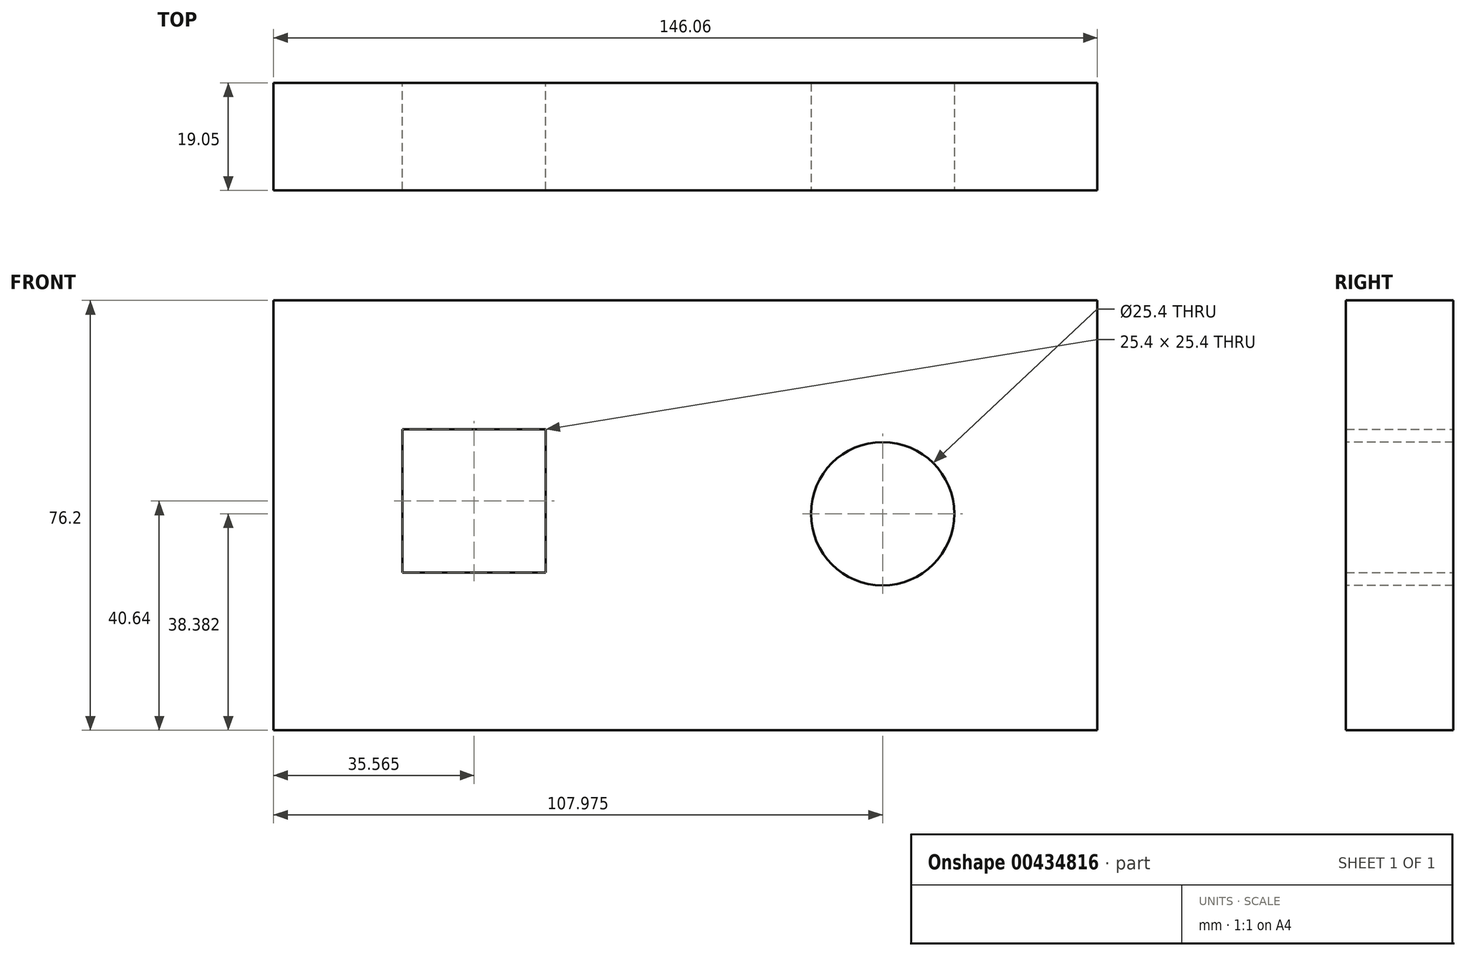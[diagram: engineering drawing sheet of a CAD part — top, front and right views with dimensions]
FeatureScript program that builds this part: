
annotation { "Feature Type Name" : "Feature", "Feature Type Description" : "" }
export const myFeature = defineFeature(function(context is Context, id is Id, definition is map)
    precondition{}
    {
        {
            var Q0;
            Q0=qCreatedBy(makeId("Front.planeOp"),FACE);
            var sketch = newSketch(context, id + "F0", { "sketchPlane" : qUnion([Q0])});
            skLineSegment(sketch, "E0.bottom", {"start": v(0, 0) * mm, "end": v(-73.03, 0) * mm});
            skLineSegment(sketch, "E0.top", {"start": v(0, 76.2) * mm, "end": v(-73.03, 76.2) * mm});
            skLineSegment(sketch, "E0.left", {"start": v(0, 0) * mm, "end": v(0, 76.2) * mm});
            skLineSegment(sketch, "E0.right", {"start": v(-73.03, 0) * mm, "end": v(-73.03, 76.2) * mm});
            skLineSegment(sketch, "E1.bottom", {"start": v(0, 0) * mm, "end": v(73.03, 0) * mm});
            skLineSegment(sketch, "E1.top", {"start": v(0, 76.2) * mm, "end": v(73.02, 76.2) * mm});
            skLineSegment(sketch, "E1.right", {"start": v(73.03, 0) * mm, "end": v(73.02, 76.2) * mm});
            skSolve(sketch);
        }
        {
            var Q0;
            Q0=makeQuery(id+"F0.imprint","IMPRINT",FACE,{"disambiguationData":[TD([[makeQuery(id+"F0.imprint","IMPRINT",EDGE,{"derivedFrom":sQuery(id+"F0.wireOp",EDGE,"E0.bottom")}),-1.0]])]});
            var sketch = newSketch(context, id + "F1", { "sketchPlane" : qUnion([Q0])});
            skLineSegment(sketch, "E2.bottom", {"start": v(-50.17, 53.34) * mm, "end": v(-24.77, 53.34) * mm});
            skLineSegment(sketch, "E2.top", {"start": v(-50.16, 27.94) * mm, "end": v(-24.77, 27.94) * mm});
            skLineSegment(sketch, "E2.left", {"start": v(-50.16, 53.34) * mm, "end": v(-50.16, 27.94) * mm});
            skLineSegment(sketch, "E2.right", {"start": v(-24.77, 53.34) * mm, "end": v(-24.76, 27.94) * mm});
            skSolve(sketch);
        }
        {
            var Q0;
            Q0=makeQuery(id+"F0.imprint","IMPRINT",FACE,{"disambiguationData":[TD([[makeQuery(id+"F0.imprint","IMPRINT",EDGE,{"derivedFrom":sQuery(id+"F0.wireOp",EDGE,"E1.bottom")}),1.0]])]});
            extrude(context, id + "F2", {"entities" : qUnion([Q0]), "depth" : 19.05 * mm});
        }
        {
            var Q0;
            Q0=makeQuery(id+"F1.imprint","IMPRINT",FACE,{"disambiguationData":[TD([[makeQuery(id+"F1.imprint","IMPRINT",EDGE,{"derivedFrom":sQuery(id+"F1.wireOp",EDGE,"E2.bottom")}),1.0]])]});
            extrude(context, id + "F3", {"entities" : qUnion([Q0]), "operationType" : NewBodyOperationType.ADD, "depth" : 19.05 * mm});
        }
        {
            var Q0;
            {var subQ0=sQuery(id+"F0.wireOp",EDGE,"E0.left");Q0=makeQuery(id+"F3.boolean.opBoolean","MERGE",FACE,{"derivedFrom":[makeQuery(id+"F2.opExtrude","CAP_FACE",FACE,{"disambiguationData":[OSD([sQuery(id+"F0.wireOp",EDGE,"E1.bottom"),sQuery(id+"F0.wireOp",EDGE,"E1.top"),subQ0,sQuery(id+"F0.wireOp",EDGE,"E1.right")])],"isStart":false}),makeQuery(id+"F3.opExtrude","CAP_FACE",FACE,{"disambiguationData":[OSD([sQuery(id+"F0.wireOp",EDGE,"E0.bottom"),sQuery(id+"F0.wireOp",EDGE,"E0.top"),sQuery(id+"F0.wireOp",EDGE,"E0.right"),subQ0,sQuery(id+"F1.wireOp",EDGE,"E2.bottom"),sQuery(id+"F1.wireOp",EDGE,"E2.top"),sQuery(id+"F1.wireOp",EDGE,"E2.left"),sQuery(id+"F1.wireOp",EDGE,"E2.right")])],"isStart":false})]});}
            var sketch = newSketch(context, id + "F4", { "sketchPlane" : qUnion([Q0])});
            skCircle(sketch, "E3", {"center": v(34.94, 38.38) * mm, "radius": 12.7 * mm});
            skSolve(sketch);
        }
        {
            var Q0;
            Q0=makeQuery(id+"F4.imprint","IMPRINT",FACE,{"disambiguationData":[TD([[makeQuery(id+"F4.imprint","IMPRINT",EDGE,{"derivedFrom":sQuery(id+"F4.wireOp",EDGE,"E3")}),1.0]])]});
            extrude(context, id + "F5", {"entities" : qUnion([Q0]), "operationType" : NewBodyOperationType.REMOVE, "oppositeDirection" : true, "depth" : 265.18 * mm});
        }
    });
